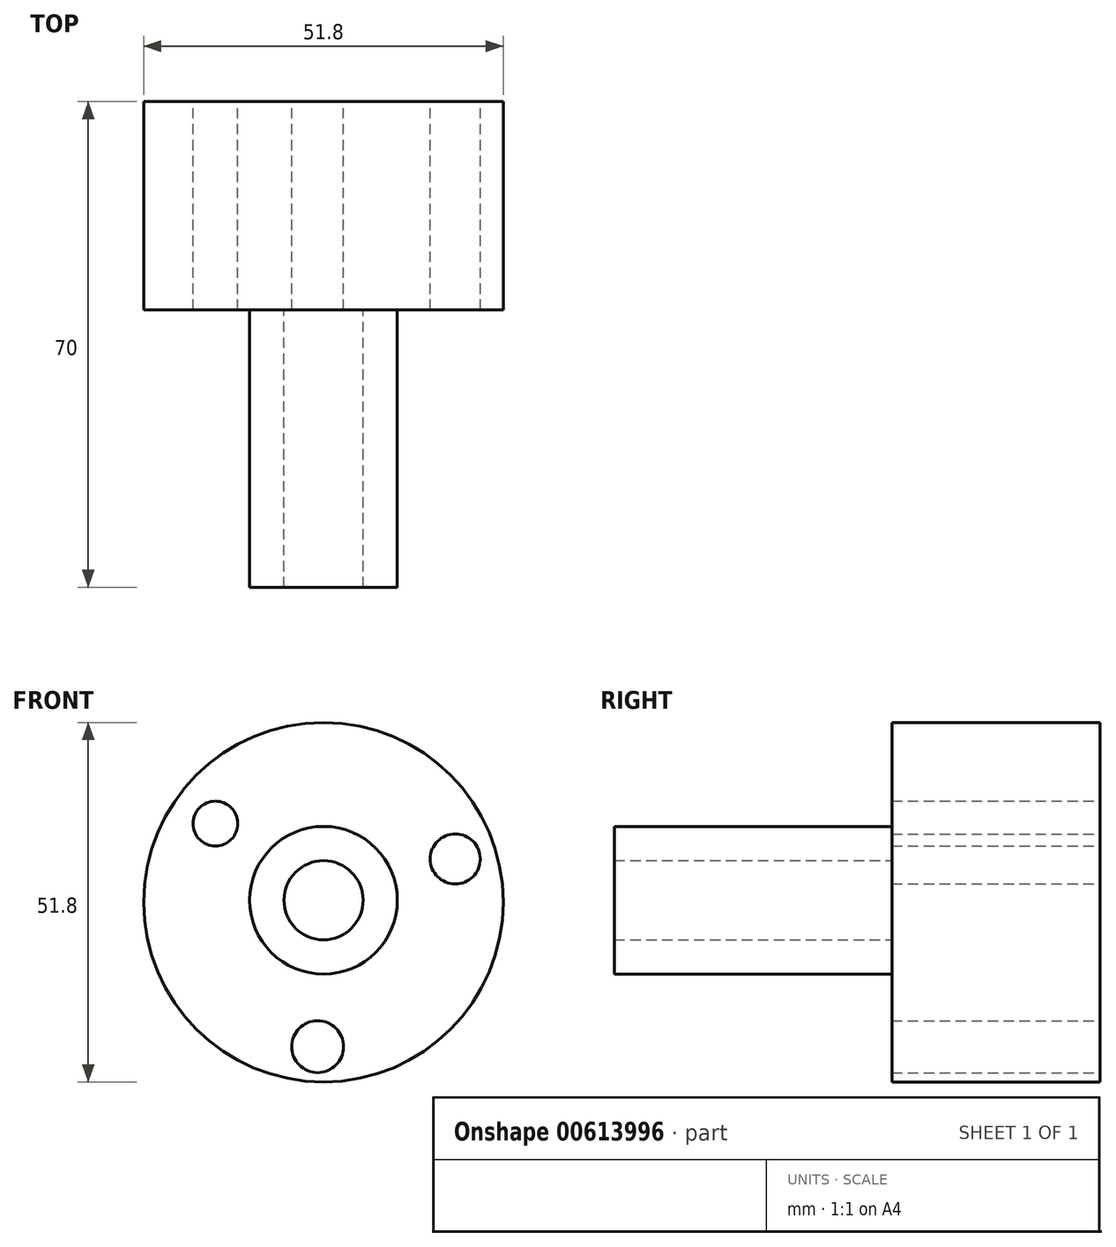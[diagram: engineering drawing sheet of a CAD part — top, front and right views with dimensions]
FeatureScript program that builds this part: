
annotation { "Feature Type Name" : "Feature", "Feature Type Description" : "" }
export const myFeature = defineFeature(function(context is Context, id is Id, definition is map)
    precondition{}
    {
        {
            var Q0;
            Q0=qCreatedBy(makeId("Front.planeOp"),FACE);
            var sketch = newSketch(context, id + "F0", { "sketchPlane" : qUnion([Q0])});
            skCircle(sketch, "E0", {"center": v(-39.8, 20.82) * mm, "radius": 25.9 * mm});
            skCircle(sketch, "E1", {"center": v(-55.38, 32.15) * mm, "radius": 3.23 * mm});
            skCircle(sketch, "E2", {"center": v(-20.82, 27.05) * mm, "radius": 3.6 * mm});
            skCircle(sketch, "E3", {"center": v(-40.65, 0) * mm, "radius": 3.74 * mm});
            skSolve(sketch);
        }
        {
            var Q0;
            Q0=qCreatedBy(makeId("Front.planeOp"),FACE);
            var sketch = newSketch(context, id + "F1", { "sketchPlane" : qUnion([Q0])});
            skCircle(sketch, "E4", {"center": v(-39.8, 21.1) * mm, "radius": 10.64 * mm});
            skCircle(sketch, "E5", {"center": v(-39.8, 21.1) * mm, "radius": 5.7 * mm});
            skSolve(sketch);
        }
        {
            var Q0;
            Q0 = qSketchRegion(id + "F1", true);
            extrude(context, id + "F2", {"entities" : qUnion([Q0]), "depth" : 70 * mm, "offsetDistance" : 25 * mm});
        }
        {
            var Q0;
            Q0 = qSketchRegion(id + "F0", true);
            extrude(context, id + "F3", {"entities" : qUnion([Q0]), "operationType" : NewBodyOperationType.ADD, "depth" : 30 * mm, "offsetDistance" : 25 * mm});
        }
    });
